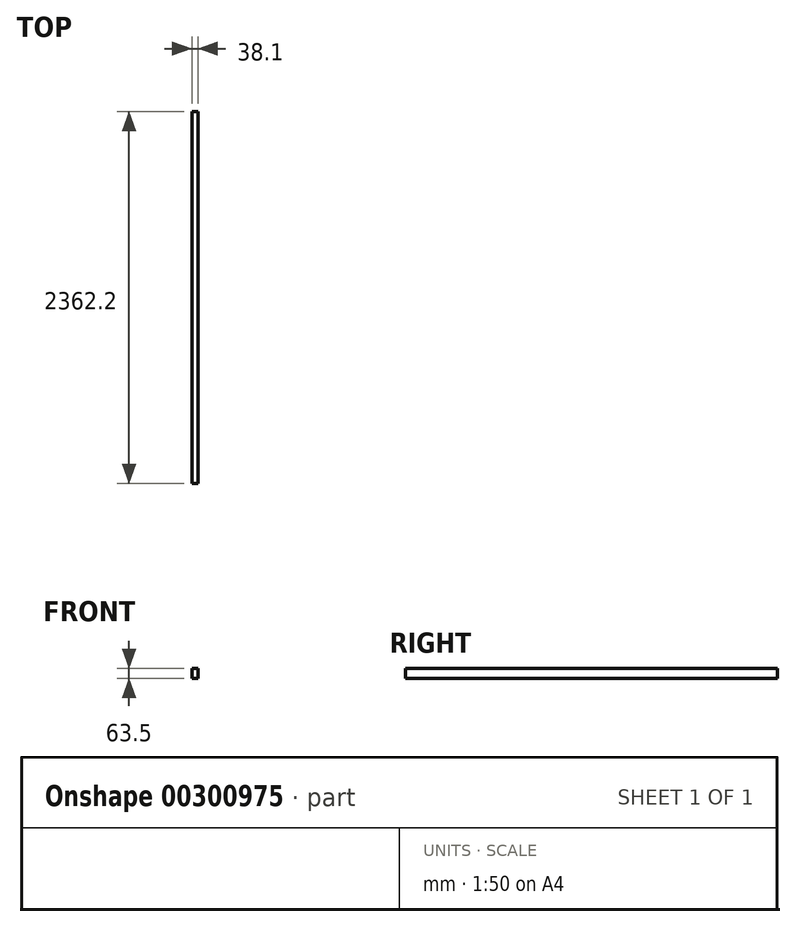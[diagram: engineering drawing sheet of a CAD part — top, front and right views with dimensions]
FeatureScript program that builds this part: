
annotation { "Feature Type Name" : "Feature", "Feature Type Description" : "" }
export const myFeature = defineFeature(function(context is Context, id is Id, definition is map)
    precondition{}
    {
        {
            var Q0;
            Q0=qCreatedBy(makeId("Top.planeOp"),FACE);
            var sketch = newSketch(context, id + "F0", { "sketchPlane" : qUnion([Q0])});
            skLineSegment(sketch, "E0.bottom", {"start": v(19.05, 1181.1) * mm, "end": v(-19.05, 1181.1) * mm});
            skLineSegment(sketch, "E0.top", {"start": v(19.05, -1181.1) * mm, "end": v(-19.05, -1181.1) * mm});
            skLineSegment(sketch, "E0.left", {"start": v(19.05, 1181.1) * mm, "end": v(19.05, -1181.1) * mm});
            skLineSegment(sketch, "E0.right", {"start": v(-19.05, 1181.1) * mm, "end": v(-19.05, -1181.1) * mm});
            skPoint(sketch, "E0.middle", {"position": v(0, 0) * mm});
            skSolve(sketch);
        }
        {
            var Q0;
            Q0 = qSketchRegion(id + "F0", true);
            extrude(context, id + "F1", {"entities" : qUnion([Q0]), "depth" : 63.5 * mm});
        }
    });
